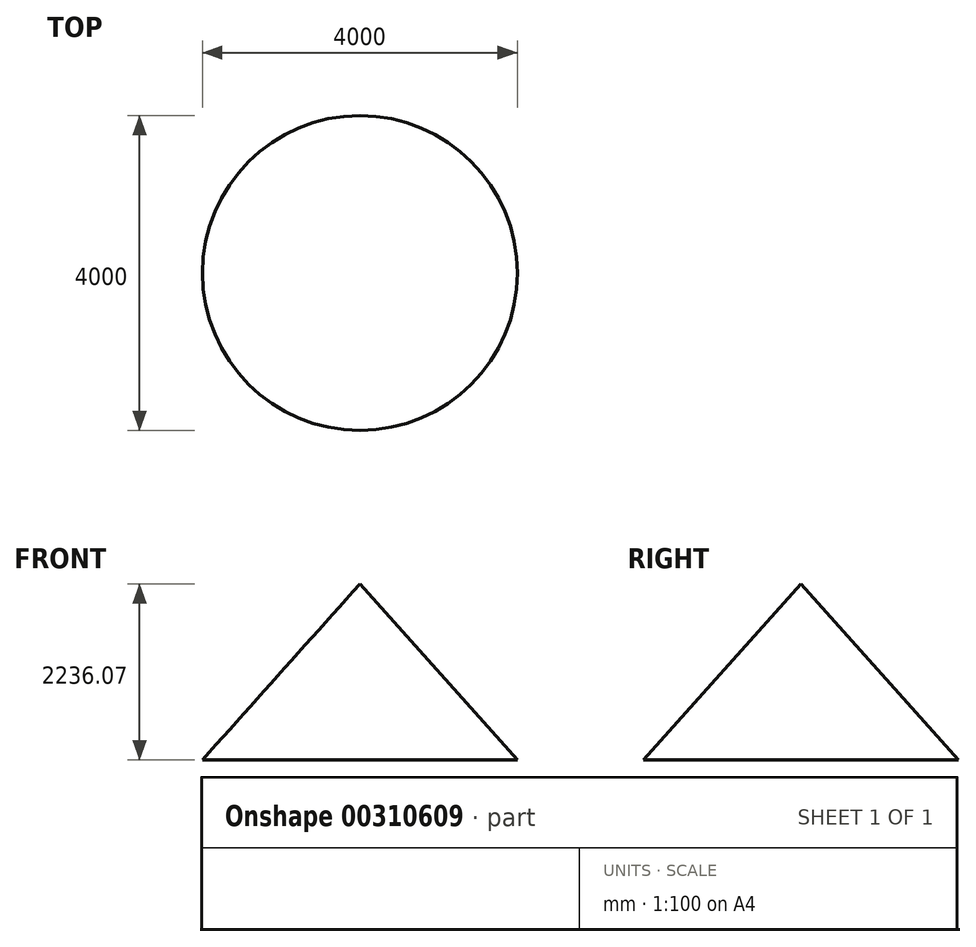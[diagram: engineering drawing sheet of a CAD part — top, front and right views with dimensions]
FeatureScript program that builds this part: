
annotation { "Feature Type Name" : "Feature", "Feature Type Description" : "" }
export const myFeature = defineFeature(function(context is Context, id is Id, definition is map)
    precondition{}
    {
        {
            var Q0;
            Q0=qCreatedBy(makeId("Right.planeOp"),FACE);
            var sketch = newSketch(context, id + "F0", { "sketchPlane" : qUnion([Q0])});
            skLineSegment(sketch, "E0", {"start": v(0, 0) * mm, "end": v(2000, 0) * mm});
            skLineSegment(sketch, "E1", {"start": v(2000, 0) * mm, "end": v(0, 2236.07) * mm});
            skLineSegment(sketch, "E2", {"start": v(0, 2236.07) * mm, "end": v(0, 0) * mm});
            skLineSegment(sketch, "E3", {"start": v(0, 2236.07) * mm, "end": v(0, 0) * mm, "construction": true});
            skSolve(sketch);
        }
        {
            var Q0;
            Q0 = qSketchRegion(id + "F0", true);
            var Q1;
            Q1=sQuery(id+"F0.wireOp",EDGE,"E2");
            revolve(context, id + "F1", {"entities" : qUnion([Q0]), "axis" : qUnion([Q1]), "revolveType" : RevolveType.FULL});
        }
    });
